# Revit family: Shower-Handshower_Kit-KOHLER-Spacity-K-R33037T_1
name_source: partatom
category: Plumbing Fixtures
units: mm (PartAtom-declared; Revit-internal decimal feet)

## family parameters
Cut with Voids When Loaded = No
Host = Face
OmniClass Number = 23.31.17.00
OmniClass Title = Showers
Part Type = Normal
Room Calculation Point = No
Round Connector Dimension = Use Diameter
Shared = No

## types (2) — shared parameters
ADA Compliant = No
Assembly Code = D2010700
CW Connection = No
Cold Water Inlet = Cold Water Inlet
Date Modified = 04/26/2024
Default Elevation = 72"
Description = Handshower and Petshower Kit
Drain Included = No
Flow Rate = 0 GPM
HW Connection = Yes
Hot Water Inlet = Hot Water Inlet
Length = 3 1/8"
Manufacturer = Kohler Co.
Master Format 2014 = 22 42 23
Master Format 2014 Name = Residential Showers
Material = Plastic
Pressure = 0.00 psi
Product Name = Spacity
Tempered Water Inlet = Tempered Water Inlet
URL = http://www.kohler.com.cn
Vent Connection = No
Waste Connection = No
Waste Water Outlet = Waste Water Outlet
WaterSense Certified = No

## per-type parameters (varying)
| type | Clip Finish | Faceplate Finish | Finish | Model | Type |
| WPT-White | Plastic-Pantone-PQ-11-4800-TCX | Kohler-Plastic-NY-Dune | Kohler-Plastic-WPT-White | K-R33037T-WPT | 2 |
| BPT-Black | Plastic-Pantone-Black_C | Silicone-Pantone-PQ-194205-TPG | Kohler-Plastic-BPT-Black | K-R33037T-BPT | 1 |

## geometry (parser evidence)
native form markers: Sweep x14
no freeform markers — native parametric forms only
